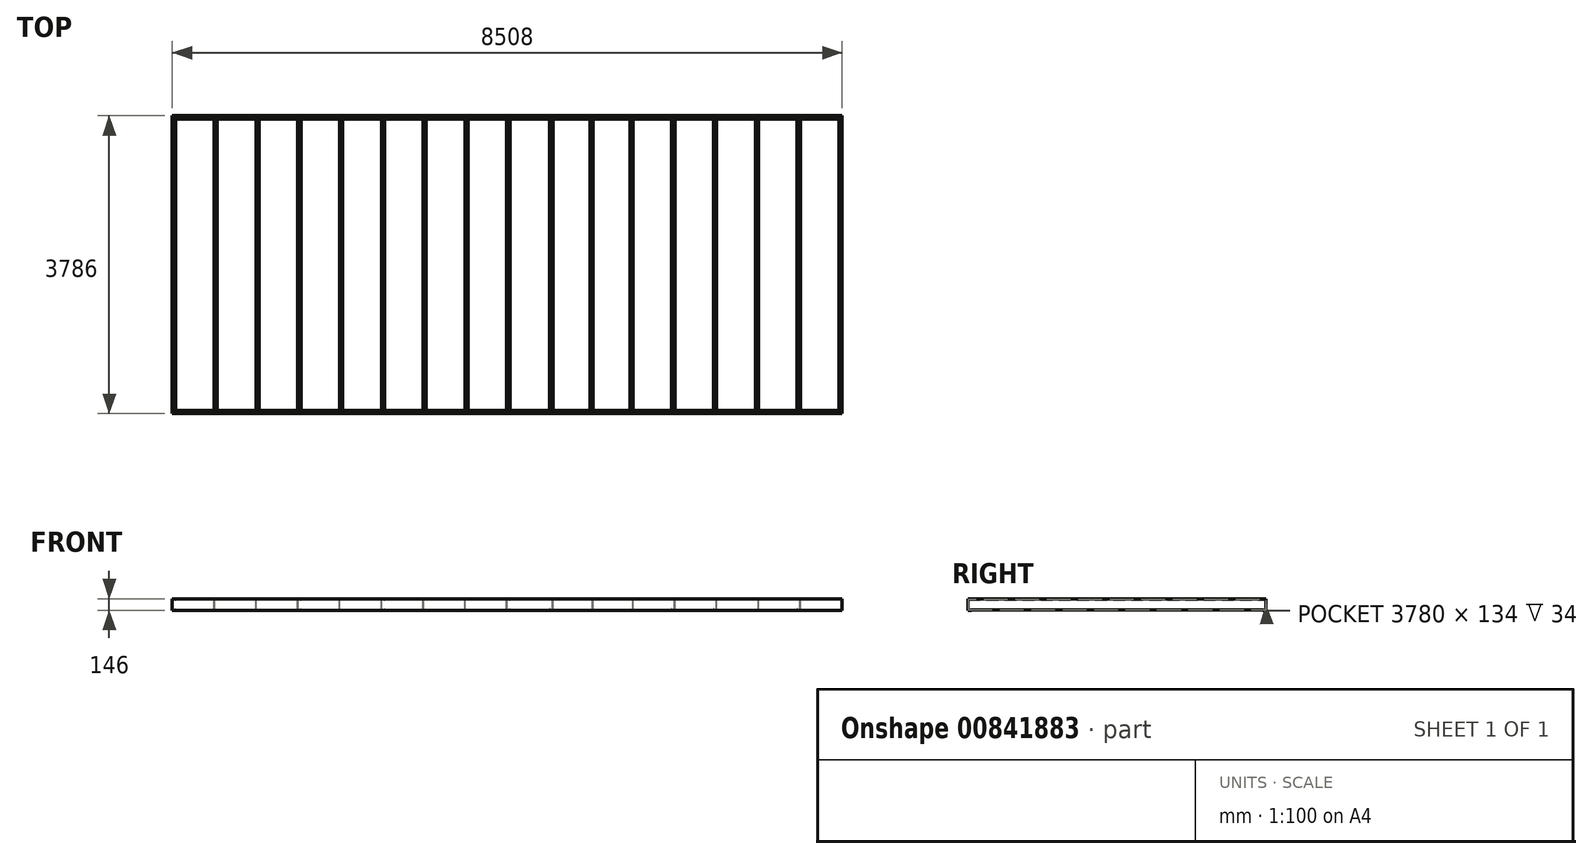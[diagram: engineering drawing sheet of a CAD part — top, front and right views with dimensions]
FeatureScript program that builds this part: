
annotation { "Feature Type Name" : "Feature", "Feature Type Description" : "" }
export const myFeature = defineFeature(function(context is Context, id is Id, definition is map)
    precondition{}
    {
        {
            var Q0;
            Q0=qCreatedBy(makeId("Front.planeOp"),FACE);
            var sketch = newSketch(context, id + "F0", { "sketchPlane" : qUnion([Q0])});
            skLineSegment(sketch, "E0", {"start": v(0, 0) * mm, "end": v(0, 140) * mm});
            skLineSegment(sketch, "E1", {"start": v(0, 140) * mm, "end": v(40, 140) * mm});
            skLineSegment(sketch, "E2", {"start": v(40, 140) * mm, "end": v(40, 128) * mm});
            skLineSegment(sketch, "E3", {"start": v(0, 0) * mm, "end": v(40, 0) * mm});
            skLineSegment(sketch, "E4", {"start": v(40, 0) * mm, "end": v(40, 12) * mm});
            skLineSegment(sketch, "E5.0", {"start": v(37, 137) * mm, "end": v(37, 128) * mm});
            skLineSegment(sketch, "E5.1", {"start": v(37, 3) * mm, "end": v(37, 12) * mm});
            skLineSegment(sketch, "E5.2", {"start": v(3, 3) * mm, "end": v(37, 3) * mm});
            skLineSegment(sketch, "E5.3", {"start": v(3, 3) * mm, "end": v(3, 137) * mm});
            skLineSegment(sketch, "E5.4", {"start": v(3, 137) * mm, "end": v(37, 137) * mm});
            skLineSegment(sketch, "E6", {"start": v(37, 128) * mm, "end": v(40, 128) * mm});
            skLineSegment(sketch, "E7", {"start": v(37, 12) * mm, "end": v(40, 12) * mm});
            skLineSegment(sketch, "E8.1.0.0", {"start": v(534, 3) * mm, "end": v(534, 137) * mm});
            skLineSegment(sketch, "E8.1.0.1", {"start": v(531, 0) * mm, "end": v(571, 0) * mm});
            skLineSegment(sketch, "E8.1.0.2", {"start": v(534, 3) * mm, "end": v(568, 3) * mm});
            skLineSegment(sketch, "E8.1.0.3", {"start": v(531, 0) * mm, "end": v(531, 140) * mm});
            skLineSegment(sketch, "E8.1.0.4", {"start": v(531, 140) * mm, "end": v(571, 140) * mm});
            skLineSegment(sketch, "E8.1.0.5", {"start": v(534, 137) * mm, "end": v(568, 137) * mm});
            skLineSegment(sketch, "E8.1.0.6", {"start": v(568, 128) * mm, "end": v(571, 128) * mm});
            skLineSegment(sketch, "E8.1.0.7", {"start": v(568, 12) * mm, "end": v(571, 12) * mm});
            skLineSegment(sketch, "E8.1.0.8", {"start": v(568, 3) * mm, "end": v(568, 12) * mm});
            skLineSegment(sketch, "E8.1.0.9", {"start": v(571, 0) * mm, "end": v(571, 12) * mm});
            skLineSegment(sketch, "E8.1.0.10", {"start": v(571, 140) * mm, "end": v(571, 128) * mm});
            skLineSegment(sketch, "E8.1.0.11", {"start": v(568, 137) * mm, "end": v(568, 128) * mm});
            skLineSegment(sketch, "E8.2.0.0", {"start": v(1065, 3) * mm, "end": v(1065, 137) * mm});
            skLineSegment(sketch, "E8.2.0.1", {"start": v(1062, 0) * mm, "end": v(1102, 0) * mm});
            skLineSegment(sketch, "E8.2.0.2", {"start": v(1065, 3) * mm, "end": v(1099, 3) * mm});
            skLineSegment(sketch, "E8.2.0.3", {"start": v(1062, 0) * mm, "end": v(1062, 140) * mm});
            skLineSegment(sketch, "E8.2.0.4", {"start": v(1062, 140) * mm, "end": v(1102, 140) * mm});
            skLineSegment(sketch, "E8.2.0.5", {"start": v(1065, 137) * mm, "end": v(1099, 137) * mm});
            skLineSegment(sketch, "E8.2.0.6", {"start": v(1099, 128) * mm, "end": v(1102, 128) * mm});
            skLineSegment(sketch, "E8.2.0.7", {"start": v(1099, 12) * mm, "end": v(1102, 12) * mm});
            skLineSegment(sketch, "E8.2.0.8", {"start": v(1099, 3) * mm, "end": v(1099, 12) * mm});
            skLineSegment(sketch, "E8.2.0.9", {"start": v(1102, 0) * mm, "end": v(1102, 12) * mm});
            skLineSegment(sketch, "E8.2.0.10", {"start": v(1102, 140) * mm, "end": v(1102, 128) * mm});
            skLineSegment(sketch, "E8.2.0.11", {"start": v(1099, 137) * mm, "end": v(1099, 128) * mm});
            skLineSegment(sketch, "E8.3.0.0", {"start": v(1596, 3) * mm, "end": v(1596, 137) * mm});
            skLineSegment(sketch, "E8.3.0.1", {"start": v(1593, 0) * mm, "end": v(1633, 0) * mm});
            skLineSegment(sketch, "E8.3.0.2", {"start": v(1596, 3) * mm, "end": v(1630, 3) * mm});
            skLineSegment(sketch, "E8.3.0.3", {"start": v(1593, 0) * mm, "end": v(1593, 140) * mm});
            skLineSegment(sketch, "E8.3.0.4", {"start": v(1593, 140) * mm, "end": v(1633, 140) * mm});
            skLineSegment(sketch, "E8.3.0.5", {"start": v(1596, 137) * mm, "end": v(1630, 137) * mm});
            skLineSegment(sketch, "E8.3.0.6", {"start": v(1630, 128) * mm, "end": v(1633, 128) * mm});
            skLineSegment(sketch, "E8.3.0.7", {"start": v(1630, 12) * mm, "end": v(1633, 12) * mm});
            skLineSegment(sketch, "E8.3.0.8", {"start": v(1630, 3) * mm, "end": v(1630, 12) * mm});
            skLineSegment(sketch, "E8.3.0.9", {"start": v(1633, 0) * mm, "end": v(1633, 12) * mm});
            skLineSegment(sketch, "E8.3.0.10", {"start": v(1633, 140) * mm, "end": v(1633, 128) * mm});
            skLineSegment(sketch, "E8.3.0.11", {"start": v(1630, 137) * mm, "end": v(1630, 128) * mm});
            skLineSegment(sketch, "E8.4.0.0", {"start": v(2127, 3) * mm, "end": v(2127, 137) * mm});
            skLineSegment(sketch, "E8.4.0.1", {"start": v(2124, 0) * mm, "end": v(2164, 0) * mm});
            skLineSegment(sketch, "E8.4.0.2", {"start": v(2127, 3) * mm, "end": v(2161, 3) * mm});
            skLineSegment(sketch, "E8.4.0.3", {"start": v(2124, 0) * mm, "end": v(2124, 140) * mm});
            skLineSegment(sketch, "E8.4.0.4", {"start": v(2124, 140) * mm, "end": v(2164, 140) * mm});
            skLineSegment(sketch, "E8.4.0.5", {"start": v(2127, 137) * mm, "end": v(2161, 137) * mm});
            skLineSegment(sketch, "E8.4.0.6", {"start": v(2161, 128) * mm, "end": v(2164, 128) * mm});
            skLineSegment(sketch, "E8.4.0.7", {"start": v(2161, 12) * mm, "end": v(2164, 12) * mm});
            skLineSegment(sketch, "E8.4.0.8", {"start": v(2161, 3) * mm, "end": v(2161, 12) * mm});
            skLineSegment(sketch, "E8.4.0.9", {"start": v(2164, 0) * mm, "end": v(2164, 12) * mm});
            skLineSegment(sketch, "E8.4.0.10", {"start": v(2164, 140) * mm, "end": v(2164, 128) * mm});
            skLineSegment(sketch, "E8.4.0.11", {"start": v(2161, 137) * mm, "end": v(2161, 128) * mm});
            skLineSegment(sketch, "E8.5.0.0", {"start": v(2658, 3) * mm, "end": v(2658, 137) * mm});
            skLineSegment(sketch, "E8.5.0.1", {"start": v(2655, 0) * mm, "end": v(2695, 0) * mm});
            skLineSegment(sketch, "E8.5.0.2", {"start": v(2658, 3) * mm, "end": v(2692, 3) * mm});
            skLineSegment(sketch, "E8.5.0.3", {"start": v(2655, 0) * mm, "end": v(2655, 140) * mm});
            skLineSegment(sketch, "E8.5.0.4", {"start": v(2655, 140) * mm, "end": v(2695, 140) * mm});
            skLineSegment(sketch, "E8.5.0.5", {"start": v(2658, 137) * mm, "end": v(2692, 137) * mm});
            skLineSegment(sketch, "E8.5.0.6", {"start": v(2692, 128) * mm, "end": v(2695, 128) * mm});
            skLineSegment(sketch, "E8.5.0.7", {"start": v(2692, 12) * mm, "end": v(2695, 12) * mm});
            skLineSegment(sketch, "E8.5.0.8", {"start": v(2692, 3) * mm, "end": v(2692, 12) * mm});
            skLineSegment(sketch, "E8.5.0.9", {"start": v(2695, 0) * mm, "end": v(2695, 12) * mm});
            skLineSegment(sketch, "E8.5.0.10", {"start": v(2695, 140) * mm, "end": v(2695, 128) * mm});
            skLineSegment(sketch, "E8.5.0.11", {"start": v(2692, 137) * mm, "end": v(2692, 128) * mm});
            skLineSegment(sketch, "E8.direction1", {"start": v(0, 0) * mm, "end": v(531, 0) * mm, "construction": true});
            skLineSegment(sketch, "E9", {"start": v(4254, 568.5) * mm, "end": v(4254, -418.8) * mm, "construction": true});
            skLineSegment(sketch, "E10.MirrorCS", {"start": v(8468, 0) * mm, "end": v(8468, 12) * mm});
            skLineSegment(sketch, "E11.MirrorCS", {"start": v(8471, 3) * mm, "end": v(8471, 12) * mm});
            skLineSegment(sketch, "E12.MirrorCS", {"start": v(8508, 0) * mm, "end": v(8468, 0) * mm});
            skLineSegment(sketch, "E13.MirrorCS", {"start": v(8471, 12) * mm, "end": v(8468, 12) * mm});
            skLineSegment(sketch, "E14.MirrorCS", {"start": v(8471, 137) * mm, "end": v(8471, 128) * mm});
            skLineSegment(sketch, "E15.MirrorCS", {"start": v(8508, 0) * mm, "end": v(8508, 140) * mm});
            skLineSegment(sketch, "E16.MirrorCS", {"start": v(8505, 3) * mm, "end": v(8471, 3) * mm});
            skLineSegment(sketch, "E17.MirrorCS", {"start": v(8508, 140) * mm, "end": v(8468, 140) * mm});
            skLineSegment(sketch, "E18.MirrorCS", {"start": v(8505, 137) * mm, "end": v(8471, 137) * mm});
            skLineSegment(sketch, "E19.MirrorCS", {"start": v(8468, 140) * mm, "end": v(8468, 128) * mm});
            skLineSegment(sketch, "E20.MirrorCS", {"start": v(8471, 128) * mm, "end": v(8468, 128) * mm});
            skLineSegment(sketch, "E21.MirrorCS", {"start": v(8505, 3) * mm, "end": v(8505, 137) * mm});
            skLineSegment(sketch, "E22.MirrorCS", {"start": v(7937, 0) * mm, "end": v(7937, 12) * mm});
            skLineSegment(sketch, "E23.MirrorCS", {"start": v(6344, 0) * mm, "end": v(6344, 12) * mm});
            skLineSegment(sketch, "E24.MirrorCS", {"start": v(7977, 0) * mm, "end": v(7937, 0) * mm});
            skLineSegment(sketch, "E25.MirrorCS", {"start": v(6912, 3) * mm, "end": v(6878, 3) * mm});
            skLineSegment(sketch, "E26.MirrorCS", {"start": v(6347, 3) * mm, "end": v(6347, 12) * mm});
            skLineSegment(sketch, "E27.MirrorCS", {"start": v(7940, 3) * mm, "end": v(7940, 12) * mm});
            skLineSegment(sketch, "E28.MirrorCS", {"start": v(6878, 3) * mm, "end": v(6878, 12) * mm});
            skLineSegment(sketch, "E29.MirrorCS", {"start": v(6381, 3) * mm, "end": v(6347, 3) * mm});
            skLineSegment(sketch, "E30.MirrorCS", {"start": v(5850, 3) * mm, "end": v(5816, 3) * mm});
            skLineSegment(sketch, "E31.MirrorCS", {"start": v(7443, 3) * mm, "end": v(7409, 3) * mm});
            skLineSegment(sketch, "E32.MirrorCS", {"start": v(5813, 0) * mm, "end": v(5813, 12) * mm});
            skLineSegment(sketch, "E33.MirrorCS", {"start": v(7974, 3) * mm, "end": v(7940, 3) * mm});
            skLineSegment(sketch, "E34.MirrorCS", {"start": v(7409, 3) * mm, "end": v(7409, 12) * mm});
            skLineSegment(sketch, "E35.MirrorCS", {"start": v(7406, 0) * mm, "end": v(7406, 12) * mm});
            skLineSegment(sketch, "E36.MirrorCS", {"start": v(7409, 12) * mm, "end": v(7406, 12) * mm});
            skLineSegment(sketch, "E37.MirrorCS", {"start": v(6347, 12) * mm, "end": v(6344, 12) * mm});
            skLineSegment(sketch, "E38.MirrorCS", {"start": v(5853, 0) * mm, "end": v(5813, 0) * mm});
            skLineSegment(sketch, "E39.MirrorCS", {"start": v(7940, 12) * mm, "end": v(7937, 12) * mm});
            skLineSegment(sketch, "E40.MirrorCS", {"start": v(5816, 12) * mm, "end": v(5813, 12) * mm});
            skLineSegment(sketch, "E41.MirrorCS", {"start": v(6384, 0) * mm, "end": v(6344, 0) * mm});
            skLineSegment(sketch, "E42.MirrorCS", {"start": v(6915, 0) * mm, "end": v(6875, 0) * mm});
            skLineSegment(sketch, "E43.MirrorCS", {"start": v(6878, 12) * mm, "end": v(6875, 12) * mm});
            skLineSegment(sketch, "E44.MirrorCS", {"start": v(6875, 0) * mm, "end": v(6875, 12) * mm});
            skLineSegment(sketch, "E45.MirrorCS", {"start": v(7446, 0) * mm, "end": v(7406, 0) * mm});
            skLineSegment(sketch, "E46.MirrorCS", {"start": v(5816, 3) * mm, "end": v(5816, 12) * mm});
            skLineSegment(sketch, "E47.MirrorCS", {"start": v(6347, 137) * mm, "end": v(6347, 128) * mm});
            skLineSegment(sketch, "E48.MirrorCS", {"start": v(7940, 137) * mm, "end": v(7940, 128) * mm});
            skLineSegment(sketch, "E49.MirrorCS", {"start": v(5816, 137) * mm, "end": v(5816, 128) * mm});
            skLineSegment(sketch, "E50.MirrorCS", {"start": v(6344, 140) * mm, "end": v(6344, 128) * mm});
            skLineSegment(sketch, "E51.MirrorCS", {"start": v(7937, 140) * mm, "end": v(7937, 128) * mm});
            skLineSegment(sketch, "E52.MirrorCS", {"start": v(6912, 137) * mm, "end": v(6878, 137) * mm});
            skLineSegment(sketch, "E53.MirrorCS", {"start": v(6875, 140) * mm, "end": v(6875, 128) * mm});
            skLineSegment(sketch, "E54.MirrorCS", {"start": v(6915, 0) * mm, "end": v(6915, 140) * mm});
            skLineSegment(sketch, "E55.MirrorCS", {"start": v(7974, 3) * mm, "end": v(7974, 137) * mm});
            skLineSegment(sketch, "E56.MirrorCS", {"start": v(5850, 137) * mm, "end": v(5816, 137) * mm});
            skLineSegment(sketch, "E57.MirrorCS", {"start": v(7406, 140) * mm, "end": v(7406, 128) * mm});
            skLineSegment(sketch, "E58.MirrorCS", {"start": v(6915, 140) * mm, "end": v(6875, 140) * mm});
            skLineSegment(sketch, "E59.MirrorCS", {"start": v(6912, 3) * mm, "end": v(6912, 137) * mm});
            skLineSegment(sketch, "E60.MirrorCS", {"start": v(7446, 140) * mm, "end": v(7406, 140) * mm});
            skLineSegment(sketch, "E61.MirrorCS", {"start": v(6878, 128) * mm, "end": v(6875, 128) * mm});
            skLineSegment(sketch, "E62.MirrorCS", {"start": v(7446, 0) * mm, "end": v(7446, 140) * mm});
            skLineSegment(sketch, "E63.MirrorCS", {"start": v(5813, 140) * mm, "end": v(5813, 128) * mm});
            skLineSegment(sketch, "E64.MirrorCS", {"start": v(6384, 0) * mm, "end": v(6384, 140) * mm});
            skLineSegment(sketch, "E65.MirrorCS", {"start": v(5850, 3) * mm, "end": v(5850, 137) * mm});
            skLineSegment(sketch, "E66.MirrorCS", {"start": v(7974, 137) * mm, "end": v(7940, 137) * mm});
            skLineSegment(sketch, "E67.MirrorCS", {"start": v(6381, 137) * mm, "end": v(6347, 137) * mm});
            skLineSegment(sketch, "E68.MirrorCS", {"start": v(6878, 137) * mm, "end": v(6878, 128) * mm});
            skLineSegment(sketch, "E69.MirrorCS", {"start": v(7409, 137) * mm, "end": v(7409, 128) * mm});
            skLineSegment(sketch, "E70.MirrorCS", {"start": v(7977, 0) * mm, "end": v(7977, 140) * mm});
            skLineSegment(sketch, "E71.MirrorCS", {"start": v(5853, 140) * mm, "end": v(5813, 140) * mm});
            skLineSegment(sketch, "E72.MirrorCS", {"start": v(7977, 140) * mm, "end": v(7937, 140) * mm});
            skLineSegment(sketch, "E73.MirrorCS", {"start": v(6381, 3) * mm, "end": v(6381, 137) * mm});
            skLineSegment(sketch, "E74.MirrorCS", {"start": v(5853, 0) * mm, "end": v(5853, 140) * mm});
            skLineSegment(sketch, "E75.MirrorCS", {"start": v(6347, 128) * mm, "end": v(6344, 128) * mm});
            skLineSegment(sketch, "E76.MirrorCS", {"start": v(7443, 3) * mm, "end": v(7443, 137) * mm});
            skLineSegment(sketch, "E77.MirrorCS", {"start": v(7443, 137) * mm, "end": v(7409, 137) * mm});
            skLineSegment(sketch, "E78.MirrorCS", {"start": v(5816, 128) * mm, "end": v(5813, 128) * mm});
            skLineSegment(sketch, "E79.MirrorCS", {"start": v(7409, 128) * mm, "end": v(7406, 128) * mm});
            skLineSegment(sketch, "E80.MirrorCS", {"start": v(6384, 140) * mm, "end": v(6344, 140) * mm});
            skLineSegment(sketch, "E81.MirrorCS", {"start": v(7940, 128) * mm, "end": v(7937, 128) * mm});
            skLineSegment(sketch, "E82.1.0.0", {"start": v(5343, 0) * mm, "end": v(5343, 140) * mm});
            skLineSegment(sketch, "E82.1.0.1", {"start": v(5340, 3) * mm, "end": v(5340, 137) * mm});
            skLineSegment(sketch, "E82.1.0.2", {"start": v(5340, 137) * mm, "end": v(5306, 137) * mm});
            skLineSegment(sketch, "E82.1.0.3", {"start": v(5343, 140) * mm, "end": v(5303, 140) * mm});
            skLineSegment(sketch, "E82.1.0.4", {"start": v(5340, 3) * mm, "end": v(5306, 3) * mm});
            skLineSegment(sketch, "E82.1.0.5", {"start": v(5343, 0) * mm, "end": v(5303, 0) * mm});
            skLineSegment(sketch, "E82.1.0.6", {"start": v(5303, 0) * mm, "end": v(5303, 12) * mm});
            skLineSegment(sketch, "E82.1.0.7", {"start": v(5306, 12) * mm, "end": v(5303, 12) * mm});
            skLineSegment(sketch, "E82.1.0.8", {"start": v(5306, 3) * mm, "end": v(5306, 12) * mm});
            skLineSegment(sketch, "E82.1.0.9", {"start": v(5306, 128) * mm, "end": v(5303, 128) * mm});
            skLineSegment(sketch, "E82.1.0.10", {"start": v(5303, 140) * mm, "end": v(5303, 128) * mm});
            skLineSegment(sketch, "E82.1.0.11", {"start": v(5306, 137) * mm, "end": v(5306, 128) * mm});
            skLineSegment(sketch, "E82.direction1", {"start": v(5813, 0) * mm, "end": v(5303, 0) * mm, "construction": true});
            skLineSegment(sketch, "E83.0.6.0", {"start": v(3189, 3) * mm, "end": v(3189, 137) * mm});
            skLineSegment(sketch, "E83.3.6.0", {"start": v(3186, 0) * mm, "end": v(3226, 0) * mm});
            skLineSegment(sketch, "E83.6.6.0", {"start": v(3189, 3) * mm, "end": v(3223, 3) * mm});
            skLineSegment(sketch, "E83.9.6.0", {"start": v(3186, 0) * mm, "end": v(3186, 140) * mm});
            skLineSegment(sketch, "E83.12.6.0", {"start": v(3186, 140) * mm, "end": v(3226, 140) * mm});
            skLineSegment(sketch, "E83.15.6.0", {"start": v(3189, 137) * mm, "end": v(3223, 137) * mm});
            skLineSegment(sketch, "E83.18.6.0", {"start": v(3223, 128) * mm, "end": v(3226, 128) * mm});
            skLineSegment(sketch, "E83.21.6.0", {"start": v(3223, 12) * mm, "end": v(3226, 12) * mm});
            skLineSegment(sketch, "E83.24.6.0", {"start": v(3223, 3) * mm, "end": v(3223, 12) * mm});
            skLineSegment(sketch, "E83.27.6.0", {"start": v(3226, 0) * mm, "end": v(3226, 12) * mm});
            skLineSegment(sketch, "E83.30.6.0", {"start": v(3226, 140) * mm, "end": v(3226, 128) * mm});
            skLineSegment(sketch, "E83.33.6.0", {"start": v(3223, 137) * mm, "end": v(3223, 128) * mm});
            skLineSegment(sketch, "E83.0.7.0", {"start": v(3720, 3) * mm, "end": v(3720, 137) * mm});
            skLineSegment(sketch, "E83.3.7.0", {"start": v(3717, 0) * mm, "end": v(3757, 0) * mm});
            skLineSegment(sketch, "E83.6.7.0", {"start": v(3720, 3) * mm, "end": v(3754, 3) * mm});
            skLineSegment(sketch, "E83.9.7.0", {"start": v(3717, 0) * mm, "end": v(3717, 140) * mm});
            skLineSegment(sketch, "E83.12.7.0", {"start": v(3717, 140) * mm, "end": v(3757, 140) * mm});
            skLineSegment(sketch, "E83.15.7.0", {"start": v(3720, 137) * mm, "end": v(3754, 137) * mm});
            skLineSegment(sketch, "E83.18.7.0", {"start": v(3754, 128) * mm, "end": v(3757, 128) * mm});
            skLineSegment(sketch, "E83.21.7.0", {"start": v(3754, 12) * mm, "end": v(3757, 12) * mm});
            skLineSegment(sketch, "E83.24.7.0", {"start": v(3754, 3) * mm, "end": v(3754, 12) * mm});
            skLineSegment(sketch, "E83.27.7.0", {"start": v(3757, 0) * mm, "end": v(3757, 12) * mm});
            skLineSegment(sketch, "E83.30.7.0", {"start": v(3757, 140) * mm, "end": v(3757, 128) * mm});
            skLineSegment(sketch, "E83.33.7.0", {"start": v(3754, 137) * mm, "end": v(3754, 128) * mm});
            skLineSegment(sketch, "E84.0.8.0", {"start": v(4251, 3) * mm, "end": v(4251, 137) * mm});
            skLineSegment(sketch, "E84.3.8.0", {"start": v(4248, 0) * mm, "end": v(4288, 0) * mm});
            skLineSegment(sketch, "E84.6.8.0", {"start": v(4251, 3) * mm, "end": v(4285, 3) * mm});
            skLineSegment(sketch, "E84.9.8.0", {"start": v(4248, 0) * mm, "end": v(4248, 140) * mm});
            skLineSegment(sketch, "E84.12.8.0", {"start": v(4248, 140) * mm, "end": v(4288, 140) * mm});
            skLineSegment(sketch, "E84.15.8.0", {"start": v(4251, 137) * mm, "end": v(4285, 137) * mm});
            skLineSegment(sketch, "E84.18.8.0", {"start": v(4285, 128) * mm, "end": v(4288, 128) * mm});
            skLineSegment(sketch, "E84.21.8.0", {"start": v(4285, 12) * mm, "end": v(4288, 12) * mm});
            skLineSegment(sketch, "E84.24.8.0", {"start": v(4285, 3) * mm, "end": v(4285, 12) * mm});
            skLineSegment(sketch, "E84.27.8.0", {"start": v(4288, 0) * mm, "end": v(4288, 12) * mm});
            skLineSegment(sketch, "E84.30.8.0", {"start": v(4288, 140) * mm, "end": v(4288, 128) * mm});
            skLineSegment(sketch, "E84.33.8.0", {"start": v(4285, 137) * mm, "end": v(4285, 128) * mm});
            skLineSegment(sketch, "E85.0.2.0", {"start": v(4833, 0) * mm, "end": v(4833, 140) * mm});
            skLineSegment(sketch, "E85.3.2.0", {"start": v(4830, 3) * mm, "end": v(4830, 137) * mm});
            skLineSegment(sketch, "E85.6.2.0", {"start": v(4830, 137) * mm, "end": v(4796, 137) * mm});
            skLineSegment(sketch, "E85.9.2.0", {"start": v(4833, 140) * mm, "end": v(4793, 140) * mm});
            skLineSegment(sketch, "E85.12.2.0", {"start": v(4830, 3) * mm, "end": v(4796, 3) * mm});
            skLineSegment(sketch, "E85.15.2.0", {"start": v(4833, 0) * mm, "end": v(4793, 0) * mm});
            skLineSegment(sketch, "E85.18.2.0", {"start": v(4793, 0) * mm, "end": v(4793, 12) * mm});
            skLineSegment(sketch, "E85.21.2.0", {"start": v(4796, 12) * mm, "end": v(4793, 12) * mm});
            skLineSegment(sketch, "E85.24.2.0", {"start": v(4796, 3) * mm, "end": v(4796, 12) * mm});
            skLineSegment(sketch, "E85.27.2.0", {"start": v(4796, 128) * mm, "end": v(4793, 128) * mm});
            skLineSegment(sketch, "E85.30.2.0", {"start": v(4793, 140) * mm, "end": v(4793, 128) * mm});
            skLineSegment(sketch, "E85.33.2.0", {"start": v(4796, 137) * mm, "end": v(4796, 128) * mm});
            skSolve(sketch);
        }
        {
            var Q0;
            Q0 = qSketchRegion(id + "F0", true);
            extrude(context, id + "F1", {"entities" : qUnion([Q0]), "depth" : 3780 * mm, "offsetDistance" : 25 * mm});
        }
        {
            var Q0;
            Q0=qCreatedBy(makeId("Right.planeOp"),FACE);
            var sketch = newSketch(context, id + "F2", { "sketchPlane" : qUnion([Q0])});
            skLineSegment(sketch, "E86", {"start": v(-40, 0) * mm, "end": v(0, 0) * mm});
            skLineSegment(sketch, "E87", {"start": v(0, 0) * mm, "end": v(0, 140) * mm});
            skLineSegment(sketch, "E88", {"start": v(0, 140) * mm, "end": v(-40, 140) * mm});
            skLineSegment(sketch, "E89.0", {"start": v(3, 143) * mm, "end": v(-40, 143) * mm});
            skLineSegment(sketch, "E89.1", {"start": v(3, -3) * mm, "end": v(3, 143) * mm});
            skLineSegment(sketch, "E89.2", {"start": v(-40, -3) * mm, "end": v(3, -3) * mm});
            skLineSegment(sketch, "E90", {"start": v(-40, 143) * mm, "end": v(-40, 140) * mm});
            skLineSegment(sketch, "E91", {"start": v(-40, 0) * mm, "end": v(-40, -3) * mm});
            skLineSegment(sketch, "E92", {"start": v(-1890, 438.93) * mm, "end": v(-1890, -447.21) * mm, "construction": true});
            skLineSegment(sketch, "E93.MirrorCS", {"start": v(-3740, 143) * mm, "end": v(-3740, 140) * mm});
            skLineSegment(sketch, "E94.MirrorCS", {"start": v(-3740, 0) * mm, "end": v(-3740, -3) * mm});
            skLineSegment(sketch, "E95.MirrorCS", {"start": v(-3740, 0) * mm, "end": v(-3780, 0) * mm});
            skLineSegment(sketch, "E96.MirrorCS", {"start": v(-3783, 143) * mm, "end": v(-3740, 143) * mm});
            skLineSegment(sketch, "E97.MirrorCS", {"start": v(-3740, -3) * mm, "end": v(-3783, -3) * mm});
            skLineSegment(sketch, "E98.MirrorCS", {"start": v(-3783, -3) * mm, "end": v(-3783, 143) * mm});
            skLineSegment(sketch, "E99.MirrorCS", {"start": v(-3780, 140) * mm, "end": v(-3740, 140) * mm});
            skLineSegment(sketch, "E100.MirrorCS", {"start": v(-3780, 0) * mm, "end": v(-3780, 140) * mm});
            skSolve(sketch);
        }
        {
            var Q0;
            Q0 = qSketchRegion(id + "F2", true);
            var Q1;
            Q1=makeQuery(id+"F1.opExtrude","SWEPT_FACE",FACE,{"disambiguationData":[OSD([sQuery(id+"F0.wireOp",EDGE,"E15.MirrorCS")])]});
            extrude(context, id + "F3", {"entities" : qUnion([Q0]), "operationType" : NewBodyOperationType.ADD, "endBound" : BoundingType.UP_TO_SURFACE, "depth" : 25 * mm, "endBoundEntityFace" : qUnion([Q1]), "offsetDistance" : 25 * mm});
        }
    });
